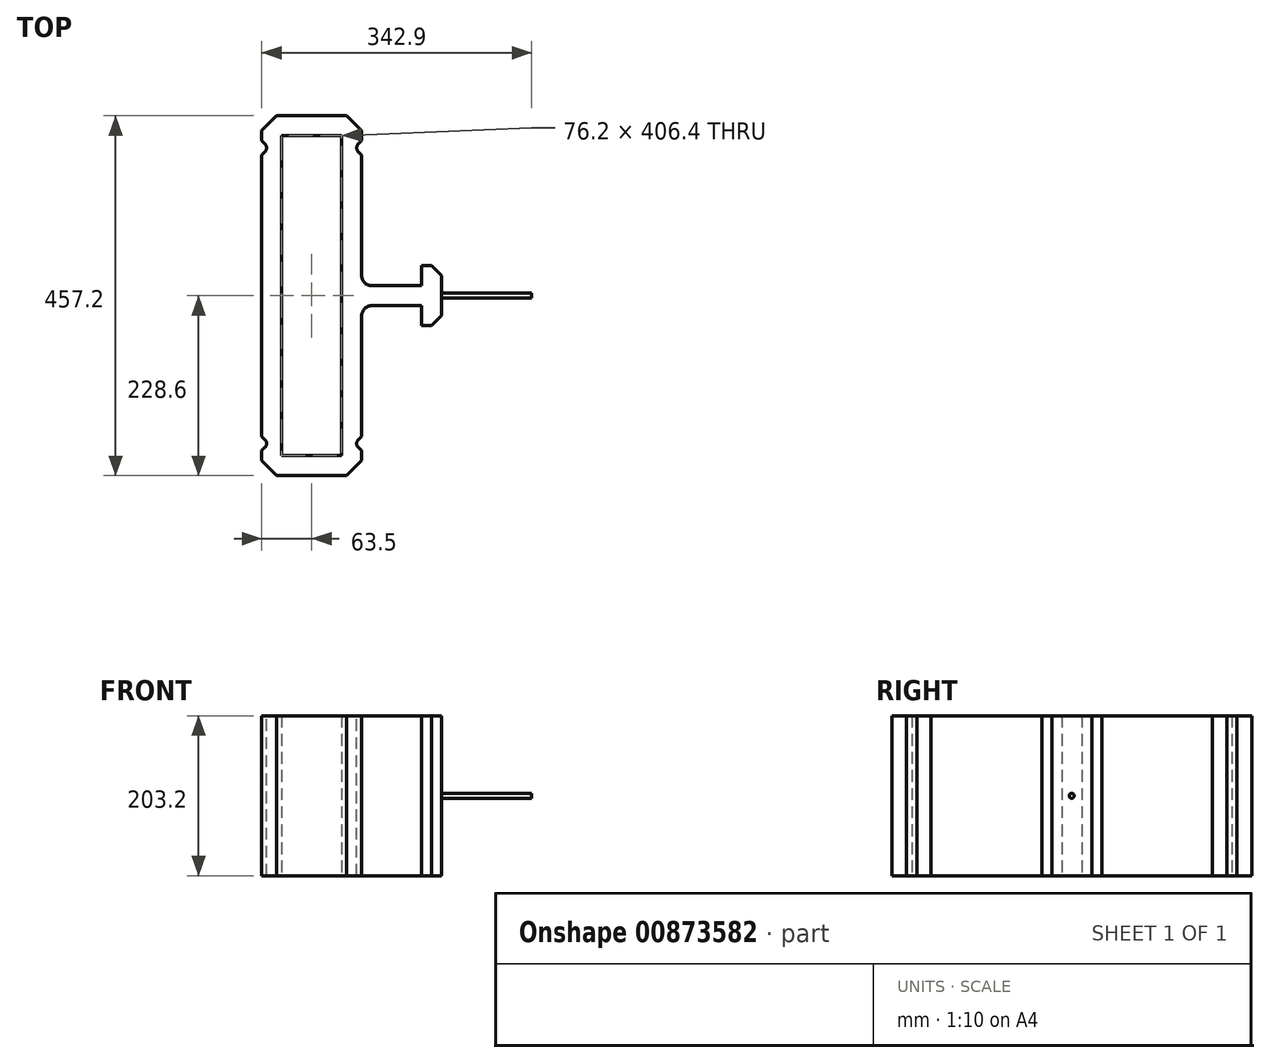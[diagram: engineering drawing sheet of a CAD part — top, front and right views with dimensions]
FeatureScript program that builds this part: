
annotation { "Feature Type Name" : "Feature", "Feature Type Description" : "" }
export const myFeature = defineFeature(function(context is Context, id is Id, definition is map)
    precondition{}
    {
        {
            var Q0;
            Q0=qCreatedBy(makeId("Top.planeOp"),FACE);
            var sketch = newSketch(context, id + "F0", { "sketchPlane" : qUnion([Q0])});
            skLineSegment(sketch, "E0.bottom", {"start": v(19.04, 0) * mm, "end": v(107.96, 0) * mm});
            skLineSegment(sketch, "E0.top", {"start": v(19.04, 457.2) * mm, "end": v(107.96, 457.2) * mm});
            skLineSegment(sketch, "E0.left", {"start": v(0, 19) * mm, "end": v(0, 31.73) * mm});
            skLineSegment(sketch, "E0.right", {"start": v(127, 19) * mm, "end": v(127, 31.73) * mm});
            skLineSegment(sketch, "E1.0", {"start": v(25.4, 25.4) * mm, "end": v(101.6, 25.4) * mm});
            skLineSegment(sketch, "E1.1", {"start": v(25.4, 25.4) * mm, "end": v(25.4, 431.8) * mm});
            skLineSegment(sketch, "E1.2", {"start": v(25.4, 431.8) * mm, "end": v(101.6, 431.8) * mm});
            skLineSegment(sketch, "E1.3", {"start": v(101.6, 25.4) * mm, "end": v(101.6, 431.8) * mm});
            skLineSegment(sketch, "E2", {"start": v(127, 425.47) * mm, "end": v(118.01, 416.47) * mm});
            skLineSegment(sketch, "E3", {"start": v(118.01, 416.47) * mm, "end": v(127, 407.5) * mm});
            skLineSegment(sketch, "E4", {"start": v(127, 425.47) * mm, "end": v(127, 438.2) * mm});
            skLineSegment(sketch, "E5", {"start": v(127, 438.2) * mm, "end": v(107.96, 457.2) * mm});
            skLineSegment(sketch, "E6", {"start": v(63.5, 431.8) * mm, "end": v(63.5, 527.51) * mm, "construction": true});
            skLineSegment(sketch, "E7.MirrorCS", {"start": v(0, 438.2) * mm, "end": v(19.04, 457.2) * mm});
            skLineSegment(sketch, "E8.MirrorCS", {"start": v(0, 425.47) * mm, "end": v(0, 438.2) * mm});
            skLineSegment(sketch, "E9.MirrorCS", {"start": v(0, 425.47) * mm, "end": v(8.99, 416.47) * mm});
            skLineSegment(sketch, "E10.MirrorCS", {"start": v(8.99, 416.47) * mm, "end": v(0, 407.5) * mm});
            skLineSegment(sketch, "E11", {"start": v(101.6, 228.6) * mm, "end": v(288.26, 228.6) * mm, "construction": true});
            skLineSegment(sketch, "E12.MirrorCS", {"start": v(0, 19) * mm, "end": v(19.04, 0) * mm});
            skLineSegment(sketch, "E13.MirrorCS", {"start": v(0, 31.73) * mm, "end": v(8.99, 40.73) * mm});
            skLineSegment(sketch, "E14.MirrorCS", {"start": v(8.99, 40.73) * mm, "end": v(0, 49.7) * mm});
            skLineSegment(sketch, "E15.MirrorCS", {"start": v(127, 19) * mm, "end": v(107.96, 0) * mm});
            skLineSegment(sketch, "E16.MirrorCS", {"start": v(127, 31.73) * mm, "end": v(118.01, 40.73) * mm});
            skLineSegment(sketch, "E17.MirrorCS", {"start": v(118.01, 40.73) * mm, "end": v(127, 49.7) * mm});
            skLineSegment(sketch, "E18.trimOffspring", {"start": v(127, 49.7) * mm, "end": v(127, 215.9) * mm});
            skLineSegment(sketch, "E19.trimOffspring", {"start": v(0, 49.7) * mm, "end": v(0, 407.5) * mm});
            skLineSegment(sketch, "E20", {"start": v(127, 241.3) * mm, "end": v(228.6, 241.3) * mm});
            skLineSegment(sketch, "E21", {"start": v(127, 215.9) * mm, "end": v(228.6, 215.9) * mm});
            skLineSegment(sketch, "E22", {"start": v(228.6, 241.3) * mm, "end": v(228.6, 215.9) * mm});
            skLineSegment(sketch, "E23.trimOffspring", {"start": v(127, 241.3) * mm, "end": v(127, 407.5) * mm});
            skLineSegment(sketch, "E24.bottom", {"start": v(228.6, 241.3) * mm, "end": v(203.2, 241.3) * mm});
            skLineSegment(sketch, "E24.top", {"start": v(228.6, 266.7) * mm, "end": v(203.2, 266.7) * mm});
            skLineSegment(sketch, "E24.left", {"start": v(228.6, 241.3) * mm, "end": v(228.6, 266.7) * mm});
            skLineSegment(sketch, "E24.right", {"start": v(203.2, 241.3) * mm, "end": v(203.2, 266.7) * mm});
            skLineSegment(sketch, "E25.MirrorCS", {"start": v(203.2, 215.9) * mm, "end": v(203.2, 190.5) * mm});
            skLineSegment(sketch, "E26.MirrorCS", {"start": v(228.6, 190.5) * mm, "end": v(203.2, 190.5) * mm});
            skLineSegment(sketch, "E27.MirrorCS", {"start": v(228.6, 215.9) * mm, "end": v(228.6, 190.5) * mm});
            skSolve(sketch);
        }
        {
            var Q0;
            Q0=qSketchRegion(id+"F0",true);
            extrude(context, id + "F1", {"entities" : qUnion([Q0]), "depth" : 203.2 * mm, "offsetDistance" : 25.4 * mm});
        }
        {
            var Q0;
            Q0=makeQuery(id+"F1.opExtrude","SWEPT_EDGE",EDGE,{"disambiguationData":[OSD([sQuery(id+"F0.wireOp",EDGE,"E2"),sQuery(id+"F0.wireOp",EDGE,"E3")])]});
            var Q1;
            Q1=makeQuery(id+"F1.opExtrude","SWEPT_EDGE",EDGE,{"disambiguationData":[OSD([sQuery(id+"F0.wireOp",EDGE,"E9.MirrorCS"),sQuery(id+"F0.wireOp",EDGE,"E10.MirrorCS")])]});
            var Q2;
            Q2=makeQuery(id+"F1.opExtrude","SWEPT_EDGE",EDGE,{"disambiguationData":[OSD([sQuery(id+"F0.wireOp",EDGE,"E13.MirrorCS"),sQuery(id+"F0.wireOp",EDGE,"E14.MirrorCS")])]});
            var Q3;
            Q3=makeQuery(id+"F1.opExtrude","SWEPT_EDGE",EDGE,{"disambiguationData":[OSD([sQuery(id+"F0.wireOp",EDGE,"E16.MirrorCS"),sQuery(id+"F0.wireOp",EDGE,"E17.MirrorCS")])]});
            fillet(context, id + "F2", {"entities" : qUnion([Q0, Q1, Q2, Q3]), "radius" : 6.35 * mm, "tangentPropagation" : true, "allowEdgeOverflow" : false});
        }
        {
            var Q0;
            Q0=makeQuery(id+"F1.opExtrude","SWEPT_EDGE",EDGE,{"disambiguationData":[OSD([sQuery(id+"F0.wireOp",EDGE,"E18.trimOffspring"),sQuery(id+"F0.wireOp",EDGE,"E21")])]});
            var Q1;
            Q1=makeQuery(id+"F1.opExtrude","SWEPT_EDGE",EDGE,{"disambiguationData":[OSD([sQuery(id+"F0.wireOp",EDGE,"E20"),sQuery(id+"F0.wireOp",EDGE,"E23.trimOffspring")])]});
            fillet(context, id + "F3", {"entities" : qUnion([Q0, Q1]), "radius" : 12.7 * mm, "tangentPropagation" : true, "allowEdgeOverflow" : false});
        }
        {
            var Q0;
            Q0=makeQuery(id+"F1.opExtrude","SWEPT_EDGE",EDGE,{"disambiguationData":[OSD([sQuery(id+"F0.wireOp",EDGE,"E26.MirrorCS"),sQuery(id+"F0.wireOp",EDGE,"E27.MirrorCS")])]});
            var Q1;
            Q1=makeQuery(id+"F1.opExtrude","SWEPT_EDGE",EDGE,{"disambiguationData":[OSD([sQuery(id+"F0.wireOp",EDGE,"E24.top"),sQuery(id+"F0.wireOp",EDGE,"E24.left")])]});
            chamfer(context, id + "F4", {"entities" : qUnion([Q0, Q1]), "width" : 12.7 * mm, "tangentPropagation" : true});
        }
        {
            var Q0;
            Q0=makeQuery(id+"F1.opExtrude","SWEPT_FACE",FACE,{"disambiguationData":[OSD([sQuery(id+"F0.wireOp",EDGE,"E22"),sQuery(id+"F0.wireOp",EDGE,"E24.left"),sQuery(id+"F0.wireOp",EDGE,"E27.MirrorCS")])]});
            var sketch = newSketch(context, id + "F5", { "sketchPlane" : qUnion([Q0])});
            skLineSegment(sketch, "E28", {"start": v(203.2, 101.6) * mm, "end": v(259.15, 101.6) * mm, "construction": true});
            skPoint(sketch, "E28.endSnap0", {"position": v(254, 101.6) * mm});
            skLineSegment(sketch, "E29", {"start": v(228.6, 203.2) * mm, "end": v(228.6, -13.84) * mm, "construction": true});
            skPoint(sketch, "E29.endSnap0", {"position": v(228.6, 0) * mm});
            skLineSegment(sketch, "E30", {"start": v(203.2, 152.4) * mm, "end": v(257.06, 152.4) * mm, "construction": true});
            skLineSegment(sketch, "E31", {"start": v(203.2, 50.8) * mm, "end": v(258.1, 50.8) * mm, "construction": true});
            skCircle(sketch, "E32", {"center": v(228.6, 152.4) * mm, "radius": 3.18 * mm, "construction": true});
            skCircle(sketch, "E33", {"center": v(228.6, 101.6) * mm, "radius": 3.18 * mm});
            skCircle(sketch, "E34", {"center": v(228.6, 50.8) * mm, "radius": 3.18 * mm, "construction": true});
            skSolve(sketch);
        }
        {
            var Q0;
            Q0 = qSketchRegion(id + "F5", true);
            extrude(context, id + "F6", {"entities" : qUnion([Q0]), "operationType" : NewBodyOperationType.ADD, "depth" : 114.3 * mm, "offsetDistance" : 25.4 * mm});
        }
    });
